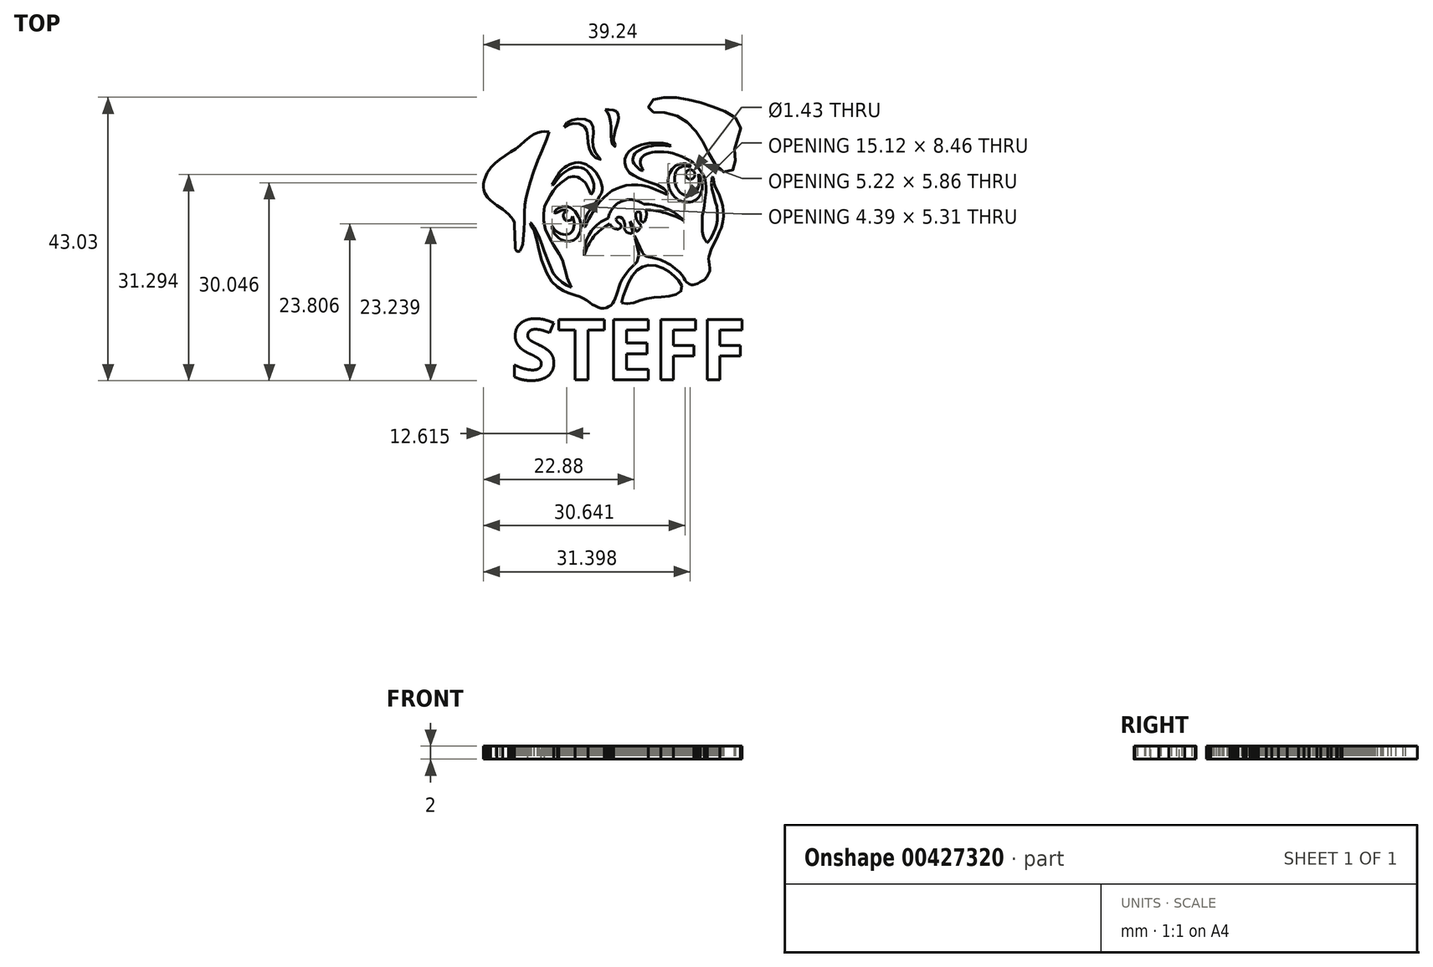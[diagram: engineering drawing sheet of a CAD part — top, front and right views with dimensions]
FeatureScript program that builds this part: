
annotation { "Feature Type Name" : "Feature", "Feature Type Description" : "" }
export const myFeature = defineFeature(function(context is Context, id is Id, definition is map)
    precondition{}
    {
        {
            var Q0;
            Q0=qCreatedBy(makeId("Top.planeOp"),FACE);
            var sketch = newSketch(context, id + "F0", { "sketchPlane" : qUnion([Q0])});
            skLineSegment(sketch, "E0", {"start": v(10.71, 26.9) * mm, "end": v(10.32, 25.78) * mm});
            skLineSegment(sketch, "E1", {"start": v(10.32, 25.78) * mm, "end": v(9.6, 24.09) * mm});
            skLineSegment(sketch, "E2", {"start": v(9.6, 24.09) * mm, "end": v(9, 22.63) * mm});
            skLineSegment(sketch, "E3", {"start": v(9, 22.63) * mm, "end": v(8.35, 20.88) * mm});
            skLineSegment(sketch, "E4", {"start": v(8.35, 20.88) * mm, "end": v(7.83, 19.32) * mm});
            skLineSegment(sketch, "E5", {"start": v(7.83, 19.32) * mm, "end": v(7.5, 18.15) * mm});
            skLineSegment(sketch, "E6", {"start": v(7.5, 18.15) * mm, "end": v(7.2, 16.98) * mm});
            skLineSegment(sketch, "E7", {"start": v(7.2, 16.98) * mm, "end": v(7.03, 15.9) * mm});
            skLineSegment(sketch, "E8", {"start": v(7.03, 15.9) * mm, "end": v(6.93, 14.65) * mm});
            skLineSegment(sketch, "E9", {"start": v(6.93, 14.65) * mm, "end": v(6.93, 13.4) * mm});
            skLineSegment(sketch, "E10", {"start": v(6.93, 13.4) * mm, "end": v(6.86, 12.03) * mm});
            skLineSegment(sketch, "E11", {"start": v(6.86, 12.03) * mm, "end": v(6.82, 11.32) * mm});
            skLineSegment(sketch, "E12", {"start": v(6.82, 11.32) * mm, "end": v(6.66, 9.88) * mm});
            skLineSegment(sketch, "E13", {"start": v(6.66, 9.88) * mm, "end": v(6.53, 9.37) * mm});
            skLineSegment(sketch, "E14", {"start": v(6.53, 9.37) * mm, "end": v(6.4, 9.06) * mm});
            skLineSegment(sketch, "E15", {"start": v(6.4, 9.06) * mm, "end": v(6.24, 8.83) * mm});
            skLineSegment(sketch, "E16", {"start": v(6.24, 8.83) * mm, "end": v(6.14, 8.77) * mm});
            skLineSegment(sketch, "E17", {"start": v(6.14, 8.77) * mm, "end": v(5.97, 8.75) * mm});
            skLineSegment(sketch, "E18", {"start": v(5.97, 8.75) * mm, "end": v(5.78, 8.8) * mm});
            skLineSegment(sketch, "E19", {"start": v(5.78, 8.8) * mm, "end": v(5.66, 8.95) * mm});
            skLineSegment(sketch, "E20", {"start": v(5.66, 8.95) * mm, "end": v(5.57, 9.16) * mm});
            skLineSegment(sketch, "E21", {"start": v(5.57, 9.16) * mm, "end": v(5.53, 9.55) * mm});
            skLineSegment(sketch, "E22", {"start": v(5.53, 9.55) * mm, "end": v(5.44, 12.77) * mm});
            skLineSegment(sketch, "E23", {"start": v(5.44, 12.77) * mm, "end": v(5.4, 13.16) * mm});
            skLineSegment(sketch, "E24", {"start": v(5.4, 13.16) * mm, "end": v(5.23, 13.6) * mm});
            skLineSegment(sketch, "E25", {"start": v(5.23, 13.6) * mm, "end": v(4.93, 14) * mm});
            skLineSegment(sketch, "E26", {"start": v(4.93, 14) * mm, "end": v(4.55, 14.4) * mm});
            skLineSegment(sketch, "E27", {"start": v(4.55, 14.4) * mm, "end": v(4.15, 14.73) * mm});
            skLineSegment(sketch, "E28", {"start": v(4.15, 14.73) * mm, "end": v(3.62, 15.16) * mm});
            skLineSegment(sketch, "E29", {"start": v(3.62, 15.16) * mm, "end": v(2.75, 15.77) * mm});
            skLineSegment(sketch, "E30", {"start": v(2.75, 15.77) * mm, "end": v(1.8, 16.54) * mm});
            skLineSegment(sketch, "E31", {"start": v(1.8, 16.54) * mm, "end": v(1.34, 16.97) * mm});
            skLineSegment(sketch, "E32", {"start": v(1.34, 16.97) * mm, "end": v(0.93, 17.65) * mm});
            skLineSegment(sketch, "E33", {"start": v(0.93, 17.65) * mm, "end": v(0.8, 18.1) * mm});
            skLineSegment(sketch, "E34", {"start": v(0.8, 18.1) * mm, "end": v(0.71, 18.48) * mm});
            skLineSegment(sketch, "E35", {"start": v(0.71, 18.48) * mm, "end": v(0.75, 19.06) * mm});
            skLineSegment(sketch, "E36", {"start": v(0.75, 19.06) * mm, "end": v(0.87, 19.56) * mm});
            skLineSegment(sketch, "E37", {"start": v(0.87, 19.56) * mm, "end": v(1.04, 20.05) * mm});
            skLineSegment(sketch, "E38", {"start": v(1.04, 20.05) * mm, "end": v(1.32, 20.73) * mm});
            skLineSegment(sketch, "E39", {"start": v(1.32, 20.73) * mm, "end": v(1.87, 21.5) * mm});
            skLineSegment(sketch, "E40", {"start": v(1.87, 21.5) * mm, "end": v(2.5, 22.16) * mm});
            skLineSegment(sketch, "E41", {"start": v(2.5, 22.16) * mm, "end": v(3.18, 22.75) * mm});
            skLineSegment(sketch, "E42", {"start": v(3.18, 22.75) * mm, "end": v(4.85, 23.86) * mm});
            skLineSegment(sketch, "E43", {"start": v(4.85, 23.86) * mm, "end": v(5.64, 24.35) * mm});
            skLineSegment(sketch, "E44", {"start": v(5.64, 24.35) * mm, "end": v(6.34, 24.92) * mm});
            skLineSegment(sketch, "E45", {"start": v(6.34, 24.92) * mm, "end": v(6.98, 25.53) * mm});
            skLineSegment(sketch, "E46", {"start": v(6.98, 25.53) * mm, "end": v(7.68, 26.08) * mm});
            skLineSegment(sketch, "E47", {"start": v(7.68, 26.08) * mm, "end": v(8.36, 26.56) * mm});
            skLineSegment(sketch, "E48", {"start": v(8.36, 26.56) * mm, "end": v(8.96, 26.8) * mm});
            skLineSegment(sketch, "E49", {"start": v(8.96, 26.8) * mm, "end": v(9.5, 26.95) * mm});
            skLineSegment(sketch, "E50", {"start": v(9.5, 26.95) * mm, "end": v(9.97, 26.97) * mm});
            skLineSegment(sketch, "E51", {"start": v(9.97, 26.97) * mm, "end": v(10.38, 26.95) * mm});
            skLineSegment(sketch, "E52", {"start": v(10.38, 26.95) * mm, "end": v(10.71, 26.9) * mm});
            skLineSegment(sketch, "E53", {"start": v(11.48, 14.68) * mm, "end": v(11.76, 15.13) * mm});
            skLineSegment(sketch, "E54", {"start": v(11.76, 15.13) * mm, "end": v(12.13, 15.39) * mm});
            skLineSegment(sketch, "E55", {"start": v(12.13, 15.39) * mm, "end": v(12.64, 15.57) * mm});
            skLineSegment(sketch, "E56", {"start": v(12.64, 15.57) * mm, "end": v(13.12, 15.6) * mm});
            skLineSegment(sketch, "E57", {"start": v(13.12, 15.6) * mm, "end": v(13.52, 15.57) * mm});
            skLineSegment(sketch, "E58", {"start": v(13.52, 15.57) * mm, "end": v(13.97, 15.39) * mm});
            skLineSegment(sketch, "E59", {"start": v(13.97, 15.39) * mm, "end": v(14.3, 15.13) * mm});
            skLineSegment(sketch, "E60", {"start": v(14.3, 15.13) * mm, "end": v(14.62, 14.84) * mm});
            skLineSegment(sketch, "E61", {"start": v(14.62, 14.84) * mm, "end": v(14.85, 14.53) * mm});
            skLineSegment(sketch, "E62", {"start": v(14.85, 14.53) * mm, "end": v(15.13, 14.06) * mm});
            skLineSegment(sketch, "E63", {"start": v(15.13, 14.06) * mm, "end": v(15.3, 13.65) * mm});
            skLineSegment(sketch, "E64", {"start": v(15.3, 13.65) * mm, "end": v(15.43, 13.2) * mm});
            skLineSegment(sketch, "E65", {"start": v(15.43, 13.2) * mm, "end": v(15.52, 12.58) * mm});
            skLineSegment(sketch, "E66", {"start": v(15.52, 12.58) * mm, "end": v(15.43, 11.9) * mm});
            skLineSegment(sketch, "E67", {"start": v(15.43, 11.9) * mm, "end": v(15.23, 11.3) * mm});
            skLineSegment(sketch, "E68", {"start": v(15.23, 11.3) * mm, "end": v(14.92, 10.84) * mm});
            skLineSegment(sketch, "E69", {"start": v(14.92, 10.84) * mm, "end": v(14.45, 10.5) * mm});
            skLineSegment(sketch, "E70", {"start": v(14.45, 10.5) * mm, "end": v(13.8, 10.3) * mm});
            skLineSegment(sketch, "E71", {"start": v(13.8, 10.3) * mm, "end": v(13.12, 10.37) * mm});
            skLineSegment(sketch, "E72", {"start": v(13.12, 10.37) * mm, "end": v(12.55, 10.56) * mm});
            skLineSegment(sketch, "E73", {"start": v(12.55, 10.56) * mm, "end": v(12.13, 10.82) * mm});
            skLineSegment(sketch, "E74", {"start": v(12.13, 10.82) * mm, "end": v(11.76, 11.16) * mm});
            skLineSegment(sketch, "E75", {"start": v(11.76, 11.16) * mm, "end": v(11.42, 11.56) * mm});
            skLineSegment(sketch, "E76", {"start": v(11.42, 11.56) * mm, "end": v(11.23, 12) * mm});
            skLineSegment(sketch, "E77", {"start": v(11.23, 12) * mm, "end": v(11.13, 12.34) * mm});
            skLineSegment(sketch, "E78", {"start": v(11.13, 12.34) * mm, "end": v(11.13, 12.63) * mm});
            skLineSegment(sketch, "E79", {"start": v(11.13, 12.63) * mm, "end": v(11.32, 12.37) * mm});
            skLineSegment(sketch, "E80", {"start": v(11.32, 12.37) * mm, "end": v(11.44, 12.16) * mm});
            skLineSegment(sketch, "E81", {"start": v(11.44, 12.16) * mm, "end": v(11.56, 12) * mm});
            skLineSegment(sketch, "E82", {"start": v(11.56, 12) * mm, "end": v(11.76, 11.81) * mm});
            skLineSegment(sketch, "E83", {"start": v(11.76, 11.81) * mm, "end": v(12, 11.67) * mm});
            skLineSegment(sketch, "E84", {"start": v(12, 11.67) * mm, "end": v(12.2, 11.54) * mm});
            skLineSegment(sketch, "E85", {"start": v(12.2, 11.54) * mm, "end": v(12.45, 11.43) * mm});
            skLineSegment(sketch, "E86", {"start": v(12.45, 11.43) * mm, "end": v(12.78, 11.35) * mm});
            skLineSegment(sketch, "E87", {"start": v(12.78, 11.35) * mm, "end": v(13.14, 11.33) * mm});
            skLineSegment(sketch, "E88", {"start": v(13.14, 11.33) * mm, "end": v(13.45, 11.37) * mm});
            skLineSegment(sketch, "E89", {"start": v(13.45, 11.37) * mm, "end": v(13.78, 11.47) * mm});
            skLineSegment(sketch, "E90", {"start": v(13.78, 11.47) * mm, "end": v(14.05, 11.66) * mm});
            skLineSegment(sketch, "E91", {"start": v(14.05, 11.66) * mm, "end": v(14.23, 11.9) * mm});
            skLineSegment(sketch, "E92", {"start": v(14.23, 11.9) * mm, "end": v(14.37, 12.2) * mm});
            skLineSegment(sketch, "E93", {"start": v(14.37, 12.2) * mm, "end": v(14.45, 12.5) * mm});
            skLineSegment(sketch, "E94", {"start": v(14.45, 12.5) * mm, "end": v(14.5, 12.82) * mm});
            skLineSegment(sketch, "E95", {"start": v(14.5, 12.82) * mm, "end": v(14.5, 13.12) * mm});
            skLineSegment(sketch, "E96", {"start": v(14.5, 13.12) * mm, "end": v(14.45, 13.43) * mm});
            skLineSegment(sketch, "E97", {"start": v(14.45, 13.43) * mm, "end": v(14.36, 13.71) * mm});
            skLineSegment(sketch, "E98", {"start": v(14.36, 13.71) * mm, "end": v(14.25, 14.1) * mm});
            skLineSegment(sketch, "E99", {"start": v(14.25, 14.1) * mm, "end": v(14.2, 13.94) * mm});
            skLineSegment(sketch, "E100", {"start": v(14.2, 13.94) * mm, "end": v(14.15, 13.72) * mm});
            skLineSegment(sketch, "E101", {"start": v(14.15, 13.72) * mm, "end": v(13.97, 13.52) * mm});
            skLineSegment(sketch, "E102", {"start": v(13.97, 13.52) * mm, "end": v(13.77, 13.44) * mm});
            skLineSegment(sketch, "E103", {"start": v(13.77, 13.44) * mm, "end": v(13.49, 13.42) * mm});
            skLineSegment(sketch, "E104", {"start": v(13.49, 13.42) * mm, "end": v(13.25, 13.48) * mm});
            skLineSegment(sketch, "E105", {"start": v(13.25, 13.48) * mm, "end": v(13.07, 13.59) * mm});
            skLineSegment(sketch, "E106", {"start": v(13.07, 13.59) * mm, "end": v(12.95, 13.78) * mm});
            skLineSegment(sketch, "E107", {"start": v(12.95, 13.78) * mm, "end": v(12.86, 14.09) * mm});
            skLineSegment(sketch, "E108", {"start": v(12.86, 14.09) * mm, "end": v(12.86, 14.4) * mm});
            skLineSegment(sketch, "E109", {"start": v(12.86, 14.4) * mm, "end": v(12.99, 14.6) * mm});
            skLineSegment(sketch, "E110", {"start": v(12.99, 14.6) * mm, "end": v(13.16, 14.77) * mm});
            skLineSegment(sketch, "E111", {"start": v(13.16, 14.77) * mm, "end": v(13.35, 14.82) * mm});
            skLineSegment(sketch, "E112", {"start": v(13.35, 14.82) * mm, "end": v(13.5, 14.82) * mm});
            skLineSegment(sketch, "E113", {"start": v(13.5, 14.82) * mm, "end": v(13.37, 15) * mm});
            skLineSegment(sketch, "E114", {"start": v(13.37, 15) * mm, "end": v(13.22, 15.03) * mm});
            skLineSegment(sketch, "E115", {"start": v(13.22, 15.03) * mm, "end": v(13, 15.03) * mm});
            skLineSegment(sketch, "E116", {"start": v(13, 15.03) * mm, "end": v(12.75, 15.03) * mm});
            skLineSegment(sketch, "E117", {"start": v(12.75, 15.03) * mm, "end": v(12.51, 14.96) * mm});
            skLineSegment(sketch, "E118", {"start": v(12.51, 14.96) * mm, "end": v(12.24, 14.85) * mm});
            skLineSegment(sketch, "E119", {"start": v(12.24, 14.85) * mm, "end": v(11.89, 14.7) * mm});
            skLineSegment(sketch, "E120", {"start": v(11.89, 14.7) * mm, "end": v(11.69, 14.64) * mm});
            skLineSegment(sketch, "E121", {"start": v(11.69, 14.64) * mm, "end": v(11.5, 14.64) * mm});
            skLineSegment(sketch, "E122", {"start": v(11.5, 14.64) * mm, "end": v(11.48, 14.68) * mm});
            skCircle(sketch, "E123", {"center": v(32.1, 20.44) * mm, "radius": 0.71 * mm});
            skLineSegment(sketch, "E124", {"start": v(32.18, 21.67) * mm, "end": v(31.86, 21.67) * mm});
            skLineSegment(sketch, "E125", {"start": v(31.86, 21.67) * mm, "end": v(31.65, 21.7) * mm});
            skLineSegment(sketch, "E126", {"start": v(31.65, 21.7) * mm, "end": v(31.35, 21.71) * mm});
            skLineSegment(sketch, "E127", {"start": v(31.35, 21.71) * mm, "end": v(31.13, 21.7) * mm});
            skLineSegment(sketch, "E128", {"start": v(31.13, 21.7) * mm, "end": v(30.87, 21.65) * mm});
            skLineSegment(sketch, "E129", {"start": v(30.87, 21.65) * mm, "end": v(30.63, 21.56) * mm});
            skLineSegment(sketch, "E130", {"start": v(30.63, 21.56) * mm, "end": v(30.45, 21.45) * mm});
            skLineSegment(sketch, "E131", {"start": v(30.45, 21.45) * mm, "end": v(30.33, 21.34) * mm});
            skLineSegment(sketch, "E132", {"start": v(30.33, 21.34) * mm, "end": v(30.2, 21.2) * mm});
            skLineSegment(sketch, "E133", {"start": v(30.2, 21.2) * mm, "end": v(30.08, 21.06) * mm});
            skLineSegment(sketch, "E134", {"start": v(30.08, 21.06) * mm, "end": v(29.95, 20.88) * mm});
            skLineSegment(sketch, "E135", {"start": v(29.95, 20.88) * mm, "end": v(29.88, 20.7) * mm});
            skLineSegment(sketch, "E136", {"start": v(29.88, 20.7) * mm, "end": v(29.82, 20.5) * mm});
            skLineSegment(sketch, "E137", {"start": v(29.82, 20.5) * mm, "end": v(29.77, 20.3) * mm});
            skLineSegment(sketch, "E138", {"start": v(29.77, 20.3) * mm, "end": v(29.73, 20.07) * mm});
            skLineSegment(sketch, "E139", {"start": v(29.73, 20.07) * mm, "end": v(29.71, 19.84) * mm});
            skLineSegment(sketch, "E140", {"start": v(29.71, 19.84) * mm, "end": v(29.71, 19.6) * mm});
            skLineSegment(sketch, "E141", {"start": v(29.71, 19.6) * mm, "end": v(29.73, 19.4) * mm});
            skLineSegment(sketch, "E142", {"start": v(29.73, 19.4) * mm, "end": v(29.75, 19.25) * mm});
            skLineSegment(sketch, "E143", {"start": v(29.75, 19.25) * mm, "end": v(29.8, 19.1) * mm});
            skLineSegment(sketch, "E144", {"start": v(29.8, 19.1) * mm, "end": v(29.84, 18.97) * mm});
            skLineSegment(sketch, "E145", {"start": v(29.84, 18.97) * mm, "end": v(29.95, 18.67) * mm});
            skLineSegment(sketch, "E146", {"start": v(29.95, 18.67) * mm, "end": v(30.07, 18.43) * mm});
            skLineSegment(sketch, "E147", {"start": v(30.07, 18.43) * mm, "end": v(30.22, 18.16) * mm});
            skLineSegment(sketch, "E148", {"start": v(30.22, 18.16) * mm, "end": v(30.39, 17.94) * mm});
            skLineSegment(sketch, "E149", {"start": v(30.39, 17.94) * mm, "end": v(30.59, 17.75) * mm});
            skLineSegment(sketch, "E150", {"start": v(30.59, 17.75) * mm, "end": v(30.81, 17.55) * mm});
            skLineSegment(sketch, "E151", {"start": v(30.81, 17.55) * mm, "end": v(31.06, 17.4) * mm});
            skLineSegment(sketch, "E152", {"start": v(31.06, 17.4) * mm, "end": v(31.3, 17.3) * mm});
            skLineSegment(sketch, "E153", {"start": v(31.3, 17.3) * mm, "end": v(31.6, 17.25) * mm});
            skLineSegment(sketch, "E154", {"start": v(31.6, 17.25) * mm, "end": v(31.95, 17.22) * mm});
            skLineSegment(sketch, "E155", {"start": v(31.95, 17.22) * mm, "end": v(32.33, 17.28) * mm});
            skLineSegment(sketch, "E156", {"start": v(32.33, 17.28) * mm, "end": v(32.62, 17.45) * mm});
            skLineSegment(sketch, "E157", {"start": v(32.62, 17.45) * mm, "end": v(32.86, 17.67) * mm});
            skLineSegment(sketch, "E158", {"start": v(32.86, 17.67) * mm, "end": v(33.1, 17.98) * mm});
            skLineSegment(sketch, "E159", {"start": v(33.1, 17.98) * mm, "end": v(33.23, 18.3) * mm});
            skLineSegment(sketch, "E160", {"start": v(33.23, 18.3) * mm, "end": v(33.36, 18.61) * mm});
            skLineSegment(sketch, "E161", {"start": v(33.36, 18.61) * mm, "end": v(33.42, 18.96) * mm});
            skLineSegment(sketch, "E162", {"start": v(33.42, 18.96) * mm, "end": v(33.42, 19.36) * mm});
            skLineSegment(sketch, "E163", {"start": v(33.42, 19.36) * mm, "end": v(33.4, 19.7) * mm});
            skLineSegment(sketch, "E164", {"start": v(33.4, 19.7) * mm, "end": v(33.33, 20.18) * mm});
            skLineSegment(sketch, "E165", {"start": v(33.33, 20.18) * mm, "end": v(33.33, 20.49) * mm});
            skLineSegment(sketch, "E166", {"start": v(33.33, 20.49) * mm, "end": v(33.42, 20.36) * mm});
            skLineSegment(sketch, "E167", {"start": v(33.42, 20.36) * mm, "end": v(33.6, 20.08) * mm});
            skLineSegment(sketch, "E168", {"start": v(33.6, 20.08) * mm, "end": v(33.77, 19.7) * mm});
            skLineSegment(sketch, "E169", {"start": v(33.77, 19.7) * mm, "end": v(33.87, 19.37) * mm});
            skLineSegment(sketch, "E170", {"start": v(33.87, 19.37) * mm, "end": v(33.96, 18.8) * mm});
            skLineSegment(sketch, "E171", {"start": v(33.96, 18.8) * mm, "end": v(33.91, 18.25) * mm});
            skLineSegment(sketch, "E172", {"start": v(33.91, 18.25) * mm, "end": v(33.77, 17.68) * mm});
            skLineSegment(sketch, "E173", {"start": v(33.77, 17.68) * mm, "end": v(33.6, 17.3) * mm});
            skLineSegment(sketch, "E174", {"start": v(33.6, 17.3) * mm, "end": v(33.3, 16.9) * mm});
            skLineSegment(sketch, "E175", {"start": v(33.3, 16.9) * mm, "end": v(33.01, 16.66) * mm});
            skLineSegment(sketch, "E176", {"start": v(33.01, 16.66) * mm, "end": v(32.67, 16.45) * mm});
            skLineSegment(sketch, "E177", {"start": v(32.67, 16.45) * mm, "end": v(32.38, 16.33) * mm});
            skLineSegment(sketch, "E178", {"start": v(32.38, 16.33) * mm, "end": v(32.07, 16.28) * mm});
            skLineSegment(sketch, "E179", {"start": v(32.07, 16.28) * mm, "end": v(31.75, 16.26) * mm});
            skLineSegment(sketch, "E180", {"start": v(31.75, 16.26) * mm, "end": v(31.45, 16.26) * mm});
            skLineSegment(sketch, "E181", {"start": v(31.45, 16.26) * mm, "end": v(31.18, 16.3) * mm});
            skLineSegment(sketch, "E182", {"start": v(31.18, 16.3) * mm, "end": v(30.91, 16.35) * mm});
            skLineSegment(sketch, "E183", {"start": v(30.91, 16.35) * mm, "end": v(30.6, 16.44) * mm});
            skLineSegment(sketch, "E184", {"start": v(30.6, 16.44) * mm, "end": v(30.33, 16.58) * mm});
            skLineSegment(sketch, "E185", {"start": v(30.33, 16.58) * mm, "end": v(30.12, 16.7) * mm});
            skLineSegment(sketch, "E186", {"start": v(30.12, 16.7) * mm, "end": v(29.9, 16.88) * mm});
            skLineSegment(sketch, "E187", {"start": v(29.9, 16.88) * mm, "end": v(29.72, 17.05) * mm});
            skLineSegment(sketch, "E188", {"start": v(29.72, 17.05) * mm, "end": v(29.55, 17.25) * mm});
            skLineSegment(sketch, "E189", {"start": v(29.55, 17.25) * mm, "end": v(29.39, 17.47) * mm});
            skLineSegment(sketch, "E190", {"start": v(29.39, 17.47) * mm, "end": v(29.27, 17.65) * mm});
            skLineSegment(sketch, "E191", {"start": v(29.27, 17.65) * mm, "end": v(29.16, 17.84) * mm});
            skLineSegment(sketch, "E192", {"start": v(29.16, 17.84) * mm, "end": v(29.03, 18.07) * mm});
            skLineSegment(sketch, "E193", {"start": v(29.03, 18.07) * mm, "end": v(28.9, 18.35) * mm});
            skLineSegment(sketch, "E194", {"start": v(28.9, 18.35) * mm, "end": v(28.83, 18.68) * mm});
            skLineSegment(sketch, "E195", {"start": v(28.83, 18.68) * mm, "end": v(28.78, 19.02) * mm});
            skLineSegment(sketch, "E196", {"start": v(28.78, 19.02) * mm, "end": v(28.74, 19.27) * mm});
            skLineSegment(sketch, "E197", {"start": v(28.74, 19.27) * mm, "end": v(28.74, 19.54) * mm});
            skLineSegment(sketch, "E198", {"start": v(28.74, 19.54) * mm, "end": v(28.78, 19.96) * mm});
            skLineSegment(sketch, "E199", {"start": v(28.78, 19.96) * mm, "end": v(28.87, 20.33) * mm});
            skLineSegment(sketch, "E200", {"start": v(28.87, 20.33) * mm, "end": v(29, 20.64) * mm});
            skLineSegment(sketch, "E201", {"start": v(29, 20.64) * mm, "end": v(29.17, 20.94) * mm});
            skLineSegment(sketch, "E202", {"start": v(29.17, 20.94) * mm, "end": v(29.39, 21.3) * mm});
            skLineSegment(sketch, "E203", {"start": v(29.39, 21.3) * mm, "end": v(29.6, 21.54) * mm});
            skLineSegment(sketch, "E204", {"start": v(29.6, 21.54) * mm, "end": v(29.87, 21.77) * mm});
            skLineSegment(sketch, "E205", {"start": v(29.87, 21.77) * mm, "end": v(30.17, 21.94) * mm});
            skLineSegment(sketch, "E206", {"start": v(30.17, 21.94) * mm, "end": v(30.56, 22.07) * mm});
            skLineSegment(sketch, "E207", {"start": v(30.56, 22.07) * mm, "end": v(31.03, 22.13) * mm});
            skLineSegment(sketch, "E208", {"start": v(31.03, 22.13) * mm, "end": v(31.41, 22.08) * mm});
            skLineSegment(sketch, "E209", {"start": v(31.41, 22.08) * mm, "end": v(31.73, 22) * mm});
            skLineSegment(sketch, "E210", {"start": v(31.73, 22) * mm, "end": v(32.11, 21.82) * mm});
            skLineSegment(sketch, "E211", {"start": v(32.11, 21.82) * mm, "end": v(32.2, 21.67) * mm});
            skLineSegment(sketch, "E212", {"start": v(32.2, 21.67) * mm, "end": v(32.18, 21.67) * mm});
            skLineSegment(sketch, "E213", {"start": v(23.61, 11.16) * mm, "end": v(24.3, 8.53) * mm});
            skLineSegment(sketch, "E214", {"start": v(24.3, 8.53) * mm, "end": v(24.3, 8.07) * mm});
            skLineSegment(sketch, "E215", {"start": v(24.3, 8.07) * mm, "end": v(24.18, 7.68) * mm});
            skLineSegment(sketch, "E216", {"start": v(24.18, 7.68) * mm, "end": v(24, 7.2) * mm});
            skLineSegment(sketch, "E217", {"start": v(24, 7.2) * mm, "end": v(23.63, 6.79) * mm});
            skLineSegment(sketch, "E218", {"start": v(23.63, 6.79) * mm, "end": v(23.22, 6.36) * mm});
            skLineSegment(sketch, "E219", {"start": v(23.22, 6.36) * mm, "end": v(22.83, 5.97) * mm});
            skLineSegment(sketch, "E220", {"start": v(22.83, 5.97) * mm, "end": v(22.42, 5.48) * mm});
            skLineSegment(sketch, "E221", {"start": v(22.42, 5.48) * mm, "end": v(22.1, 5.04) * mm});
            skLineSegment(sketch, "E222", {"start": v(22.1, 5.04) * mm, "end": v(21.8, 4.55) * mm});
            skLineSegment(sketch, "E223", {"start": v(21.8, 4.55) * mm, "end": v(21.51, 3.96) * mm});
            skLineSegment(sketch, "E224", {"start": v(21.51, 3.96) * mm, "end": v(21.3, 3.36) * mm});
            skLineSegment(sketch, "E225", {"start": v(21.3, 3.36) * mm, "end": v(21.1, 2.72) * mm});
            skLineSegment(sketch, "E226", {"start": v(21.1, 2.72) * mm, "end": v(20.94, 2.2) * mm});
            skLineSegment(sketch, "E227", {"start": v(20.94, 2.2) * mm, "end": v(20.73, 1.67) * mm});
            skLineSegment(sketch, "E228", {"start": v(20.73, 1.67) * mm, "end": v(20.54, 1.22) * mm});
            skLineSegment(sketch, "E229", {"start": v(20.54, 1.22) * mm, "end": v(20.36, 0.91) * mm});
            skLineSegment(sketch, "E230", {"start": v(20.36, 0.91) * mm, "end": v(20.1, 0.6) * mm});
            skLineSegment(sketch, "E231", {"start": v(20.1, 0.6) * mm, "end": v(19.72, 0.36) * mm});
            skLineSegment(sketch, "E232", {"start": v(19.72, 0.36) * mm, "end": v(19.42, 0.2) * mm});
            skLineSegment(sketch, "E233", {"start": v(19.42, 0.2) * mm, "end": v(19, 0.15) * mm});
            skLineSegment(sketch, "E234", {"start": v(19, 0.15) * mm, "end": v(18.59, 0.15) * mm});
            skLineSegment(sketch, "E235", {"start": v(18.59, 0.15) * mm, "end": v(18.16, 0.3) * mm});
            skLineSegment(sketch, "E236", {"start": v(18.16, 0.3) * mm, "end": v(17.7, 0.49) * mm});
            skLineSegment(sketch, "E237", {"start": v(17.7, 0.49) * mm, "end": v(17.23, 0.7) * mm});
            skLineSegment(sketch, "E238", {"start": v(17.23, 0.7) * mm, "end": v(16.9, 0.98) * mm});
            skLineSegment(sketch, "E239", {"start": v(23.61, 11.16) * mm, "end": v(24.87, 8.6) * mm});
            skLineSegment(sketch, "E240", {"start": v(24.87, 8.6) * mm, "end": v(25.05, 8.35) * mm});
            skLineSegment(sketch, "E241", {"start": v(25.05, 8.35) * mm, "end": v(25.25, 8.14) * mm});
            skLineSegment(sketch, "E242", {"start": v(25.25, 8.14) * mm, "end": v(25.47, 8) * mm});
            skLineSegment(sketch, "E243", {"start": v(25.47, 8) * mm, "end": v(25.71, 7.95) * mm});
            skLineSegment(sketch, "E244", {"start": v(25.71, 7.95) * mm, "end": v(26.04, 7.89) * mm});
            skLineSegment(sketch, "E245", {"start": v(26.04, 7.89) * mm, "end": v(26.37, 7.81) * mm});
            skLineSegment(sketch, "E246", {"start": v(26.37, 7.81) * mm, "end": v(26.66, 7.75) * mm});
            skLineSegment(sketch, "E247", {"start": v(26.66, 7.75) * mm, "end": v(27.15, 7.61) * mm});
            skLineSegment(sketch, "E248", {"start": v(27.15, 7.61) * mm, "end": v(27.56, 7.48) * mm});
            skLineSegment(sketch, "E249", {"start": v(27.56, 7.48) * mm, "end": v(27.97, 7.32) * mm});
            skLineSegment(sketch, "E250", {"start": v(27.97, 7.32) * mm, "end": v(28.3, 7.15) * mm});
            skLineSegment(sketch, "E251", {"start": v(28.3, 7.15) * mm, "end": v(28.72, 6.95) * mm});
            skLineSegment(sketch, "E252", {"start": v(28.72, 6.95) * mm, "end": v(29.08, 6.73) * mm});
            skLineSegment(sketch, "E253", {"start": v(29.08, 6.73) * mm, "end": v(29.45, 6.48) * mm});
            skLineSegment(sketch, "E254", {"start": v(29.45, 6.48) * mm, "end": v(29.78, 6.2) * mm});
            skLineSegment(sketch, "E255", {"start": v(29.78, 6.2) * mm, "end": v(30.11, 5.9) * mm});
            skLineSegment(sketch, "E256", {"start": v(30.11, 5.9) * mm, "end": v(30.43, 5.63) * mm});
            skLineSegment(sketch, "E257", {"start": v(30.43, 5.63) * mm, "end": v(30.72, 5.33) * mm});
            skLineSegment(sketch, "E258", {"start": v(30.72, 5.33) * mm, "end": v(30.95, 5.08) * mm});
            skLineSegment(sketch, "E259", {"start": v(30.95, 5.08) * mm, "end": v(31.16, 4.72) * mm});
            skLineSegment(sketch, "E260", {"start": v(31.16, 4.72) * mm, "end": v(31.33, 4.42) * mm});
            skLineSegment(sketch, "E261", {"start": v(31.33, 4.42) * mm, "end": v(31.53, 4.15) * mm});
            skLineSegment(sketch, "E262", {"start": v(31.53, 4.15) * mm, "end": v(31.75, 3.95) * mm});
            skLineSegment(sketch, "E263", {"start": v(31.75, 3.95) * mm, "end": v(31.97, 3.8) * mm});
            skLineSegment(sketch, "E264", {"start": v(31.97, 3.8) * mm, "end": v(32.27, 3.7) * mm});
            skLineSegment(sketch, "E265", {"start": v(32.27, 3.7) * mm, "end": v(32.55, 3.7) * mm});
            skLineSegment(sketch, "E266", {"start": v(32.55, 3.7) * mm, "end": v(32.81, 3.73) * mm});
            skLineSegment(sketch, "E267", {"start": v(16.9, 0.98) * mm, "end": v(16.41, 1.3) * mm});
            skLineSegment(sketch, "E268", {"start": v(16.41, 1.3) * mm, "end": v(15.84, 1.65) * mm});
            skLineSegment(sketch, "E269", {"start": v(15.84, 1.65) * mm, "end": v(15.34, 1.92) * mm});
            skLineSegment(sketch, "E270", {"start": v(15.34, 1.92) * mm, "end": v(14.69, 2.13) * mm});
            skLineSegment(sketch, "E271", {"start": v(14.69, 2.13) * mm, "end": v(14.15, 2.3) * mm});
            skLineSegment(sketch, "E272", {"start": v(14.15, 2.3) * mm, "end": v(13.54, 2.5) * mm});
            skLineSegment(sketch, "E273", {"start": v(13.54, 2.5) * mm, "end": v(12.86, 2.8) * mm});
            skLineSegment(sketch, "E274", {"start": v(12.86, 2.8) * mm, "end": v(11.94, 3.4) * mm});
            skLineSegment(sketch, "E275", {"start": v(11.94, 3.4) * mm, "end": v(11.07, 4.23) * mm});
            skLineSegment(sketch, "E276", {"start": v(11.07, 4.23) * mm, "end": v(10.3, 5.53) * mm});
            skLineSegment(sketch, "E277", {"start": v(10.3, 5.53) * mm, "end": v(9.58, 7.4) * mm});
            skLineSegment(sketch, "E278", {"start": v(9.58, 7.4) * mm, "end": v(9.2, 8.88) * mm});
            skLineSegment(sketch, "E279", {"start": v(9.2, 8.88) * mm, "end": v(8.86, 10.34) * mm});
            skLineSegment(sketch, "E280", {"start": v(8.86, 10.34) * mm, "end": v(8.38, 11.92) * mm});
            skLineSegment(sketch, "E281", {"start": v(8.38, 11.92) * mm, "end": v(7.94, 12.58) * mm});
            skLineSegment(sketch, "E282", {"start": v(7.94, 12.58) * mm, "end": v(7.8, 13.12) * mm});
            skLineSegment(sketch, "E283", {"start": v(7.8, 13.12) * mm, "end": v(7.93, 13.1) * mm});
            skLineSegment(sketch, "E284", {"start": v(7.93, 13.1) * mm, "end": v(8.43, 12.48) * mm});
            skLineSegment(sketch, "E285", {"start": v(8.43, 12.48) * mm, "end": v(9.11, 11.13) * mm});
            skLineSegment(sketch, "E286", {"start": v(9.11, 11.13) * mm, "end": v(9.63, 9.8) * mm});
            skLineSegment(sketch, "E287", {"start": v(9.63, 9.8) * mm, "end": v(9.93, 8.8) * mm});
            skLineSegment(sketch, "E288", {"start": v(9.93, 8.8) * mm, "end": v(10.61, 7.04) * mm});
            skLineSegment(sketch, "E289", {"start": v(10.61, 7.04) * mm, "end": v(11.33, 5.41) * mm});
            skLineSegment(sketch, "E290", {"start": v(11.33, 5.41) * mm, "end": v(11.9, 4.75) * mm});
            skLineSegment(sketch, "E291", {"start": v(11.9, 4.75) * mm, "end": v(12.67, 4.1) * mm});
            skLineSegment(sketch, "E292", {"start": v(12.67, 4.1) * mm, "end": v(13.33, 3.6) * mm});
            skLineSegment(sketch, "E293", {"start": v(13.33, 3.6) * mm, "end": v(14.03, 3.3) * mm});
            skLineSegment(sketch, "E294", {"start": v(14.03, 3.3) * mm, "end": v(13.42, 4.75) * mm});
            skLineSegment(sketch, "E295", {"start": v(13.42, 4.75) * mm, "end": v(13.23, 5.58) * mm});
            skLineSegment(sketch, "E296", {"start": v(13.23, 5.58) * mm, "end": v(12.98, 6.5) * mm});
            skLineSegment(sketch, "E297", {"start": v(12.98, 6.5) * mm, "end": v(12.72, 7.43) * mm});
            skLineSegment(sketch, "E298", {"start": v(12.72, 7.43) * mm, "end": v(12.23, 8.42) * mm});
            skLineSegment(sketch, "E299", {"start": v(12.23, 8.42) * mm, "end": v(11.8, 9.08) * mm});
            skLineSegment(sketch, "E300", {"start": v(11.8, 9.08) * mm, "end": v(11.33, 9.76) * mm});
            skLineSegment(sketch, "E301", {"start": v(11.33, 9.76) * mm, "end": v(10.75, 10.82) * mm});
            skLineSegment(sketch, "E302", {"start": v(10.75, 10.82) * mm, "end": v(10.1, 12.14) * mm});
            skLineSegment(sketch, "E303", {"start": v(10.1, 12.14) * mm, "end": v(9.85, 13.44) * mm});
            skLineSegment(sketch, "E304", {"start": v(9.85, 13.44) * mm, "end": v(9.85, 14.5) * mm});
            skLineSegment(sketch, "E305", {"start": v(9.85, 14.5) * mm, "end": v(9.98, 15.64) * mm});
            skLineSegment(sketch, "E306", {"start": v(9.98, 15.64) * mm, "end": v(10.43, 16.46) * mm});
            skLineSegment(sketch, "E307", {"start": v(10.43, 16.46) * mm, "end": v(10.86, 17.3) * mm});
            skLineSegment(sketch, "E308", {"start": v(10.86, 17.3) * mm, "end": v(11.32, 17.97) * mm});
            skLineSegment(sketch, "E309", {"start": v(11.32, 17.97) * mm, "end": v(11.8, 18.56) * mm});
            skLineSegment(sketch, "E310", {"start": v(11.8, 18.56) * mm, "end": v(12.42, 19.14) * mm});
            skLineSegment(sketch, "E311", {"start": v(12.42, 19.14) * mm, "end": v(13.14, 19.63) * mm});
            skLineSegment(sketch, "E312", {"start": v(13.14, 19.63) * mm, "end": v(13.64, 19.98) * mm});
            skLineSegment(sketch, "E313", {"start": v(13.64, 19.98) * mm, "end": v(14.22, 20.15) * mm});
            skLineSegment(sketch, "E314", {"start": v(14.22, 20.15) * mm, "end": v(14.63, 20.15) * mm});
            skLineSegment(sketch, "E315", {"start": v(14.63, 20.15) * mm, "end": v(15.04, 20.04) * mm});
            skLineSegment(sketch, "E316", {"start": v(15.04, 20.04) * mm, "end": v(15.33, 19.88) * mm});
            skLineSegment(sketch, "E317", {"start": v(15.33, 19.88) * mm, "end": v(15.78, 19.58) * mm});
            skLineSegment(sketch, "E318", {"start": v(15.78, 19.58) * mm, "end": v(16.2, 19.16) * mm});
            skLineSegment(sketch, "E319", {"start": v(16.2, 19.16) * mm, "end": v(16.52, 18.57) * mm});
            skLineSegment(sketch, "E320", {"start": v(16.52, 18.57) * mm, "end": v(16.77, 18.07) * mm});
            skLineSegment(sketch, "E321", {"start": v(16.77, 18.07) * mm, "end": v(16.91, 17.67) * mm});
            skLineSegment(sketch, "E322", {"start": v(16.91, 17.67) * mm, "end": v(17.04, 17.49) * mm});
            skLineSegment(sketch, "E323", {"start": v(17.04, 17.49) * mm, "end": v(17.15, 17.52) * mm});
            skLineSegment(sketch, "E324", {"start": v(17.15, 17.52) * mm, "end": v(17.34, 17.76) * mm});
            skLineSegment(sketch, "E325", {"start": v(17.34, 17.76) * mm, "end": v(17.47, 18.4) * mm});
            skLineSegment(sketch, "E326", {"start": v(17.47, 18.4) * mm, "end": v(17.47, 19) * mm});
            skLineSegment(sketch, "E327", {"start": v(17.47, 19) * mm, "end": v(17.25, 19.78) * mm});
            skLineSegment(sketch, "E328", {"start": v(17.25, 19.78) * mm, "end": v(17, 20.24) * mm});
            skLineSegment(sketch, "E329", {"start": v(17, 20.24) * mm, "end": v(16.68, 20.69) * mm});
            skLineSegment(sketch, "E330", {"start": v(16.68, 20.69) * mm, "end": v(16.39, 21) * mm});
            skLineSegment(sketch, "E331", {"start": v(16.39, 21) * mm, "end": v(15.98, 21.32) * mm});
            skLineSegment(sketch, "E332", {"start": v(15.98, 21.32) * mm, "end": v(15.57, 21.47) * mm});
            skLineSegment(sketch, "E333", {"start": v(15.57, 21.47) * mm, "end": v(15.2, 21.56) * mm});
            skLineSegment(sketch, "E334", {"start": v(15.2, 21.56) * mm, "end": v(14.84, 21.56) * mm});
            skLineSegment(sketch, "E335", {"start": v(14.84, 21.56) * mm, "end": v(14.43, 21.51) * mm});
            skLineSegment(sketch, "E336", {"start": v(14.43, 21.51) * mm, "end": v(14.1, 21.4) * mm});
            skLineSegment(sketch, "E337", {"start": v(14.1, 21.4) * mm, "end": v(13.65, 21.24) * mm});
            skLineSegment(sketch, "E338", {"start": v(13.65, 21.24) * mm, "end": v(13.26, 20.96) * mm});
            skLineSegment(sketch, "E339", {"start": v(13.26, 20.96) * mm, "end": v(12.91, 20.72) * mm});
            skLineSegment(sketch, "E340", {"start": v(12.91, 20.72) * mm, "end": v(12.62, 20.47) * mm});
            skLineSegment(sketch, "E341", {"start": v(12.62, 20.47) * mm, "end": v(12.3, 20.13) * mm});
            skLineSegment(sketch, "E342", {"start": v(12.3, 20.13) * mm, "end": v(12.04, 19.81) * mm});
            skLineSegment(sketch, "E343", {"start": v(12.04, 19.81) * mm, "end": v(11.8, 19.52) * mm});
            skLineSegment(sketch, "E344", {"start": v(11.8, 19.52) * mm, "end": v(11.53, 19.14) * mm});
            skLineSegment(sketch, "E345", {"start": v(11.53, 19.14) * mm, "end": v(11.22, 18.77) * mm});
            skLineSegment(sketch, "E346", {"start": v(11.22, 18.77) * mm, "end": v(11.13, 18.84) * mm});
            skLineSegment(sketch, "E347", {"start": v(11.13, 18.84) * mm, "end": v(11.52, 19.52) * mm});
            skLineSegment(sketch, "E348", {"start": v(11.52, 19.52) * mm, "end": v(11.89, 20.15) * mm});
            skLineSegment(sketch, "E349", {"start": v(11.89, 20.15) * mm, "end": v(12.3, 20.84) * mm});
            skLineSegment(sketch, "E350", {"start": v(12.3, 20.84) * mm, "end": v(12.68, 21.2) * mm});
            skLineSegment(sketch, "E351", {"start": v(12.68, 21.2) * mm, "end": v(13.06, 21.5) * mm});
            skLineSegment(sketch, "E352", {"start": v(13.06, 21.5) * mm, "end": v(13.39, 21.75) * mm});
            skLineSegment(sketch, "E353", {"start": v(13.39, 21.75) * mm, "end": v(13.78, 21.98) * mm});
            skLineSegment(sketch, "E354", {"start": v(13.78, 21.98) * mm, "end": v(14.17, 22.13) * mm});
            skLineSegment(sketch, "E355", {"start": v(14.17, 22.13) * mm, "end": v(14.65, 22.24) * mm});
            skLineSegment(sketch, "E356", {"start": v(14.65, 22.24) * mm, "end": v(15.1, 22.29) * mm});
            skLineSegment(sketch, "E357", {"start": v(15.1, 22.29) * mm, "end": v(15.5, 22.24) * mm});
            skLineSegment(sketch, "E358", {"start": v(15.5, 22.24) * mm, "end": v(15.97, 22.13) * mm});
            skLineSegment(sketch, "E359", {"start": v(15.97, 22.13) * mm, "end": v(16.37, 21.96) * mm});
            skLineSegment(sketch, "E360", {"start": v(16.37, 21.96) * mm, "end": v(16.68, 21.75) * mm});
            skLineSegment(sketch, "E361", {"start": v(16.68, 21.75) * mm, "end": v(17.1, 21.45) * mm});
            skLineSegment(sketch, "E362", {"start": v(17.1, 21.45) * mm, "end": v(17.46, 21.1) * mm});
            skLineSegment(sketch, "E363", {"start": v(17.46, 21.1) * mm, "end": v(17.78, 20.75) * mm});
            skLineSegment(sketch, "E364", {"start": v(17.78, 20.75) * mm, "end": v(18.07, 20.34) * mm});
            skLineSegment(sketch, "E365", {"start": v(18.07, 20.34) * mm, "end": v(18.3, 19.9) * mm});
            skLineSegment(sketch, "E366", {"start": v(18.3, 19.9) * mm, "end": v(18.5, 19.49) * mm});
            skLineSegment(sketch, "E367", {"start": v(18.5, 19.49) * mm, "end": v(18.65, 19.01) * mm});
            skLineSegment(sketch, "E368", {"start": v(18.65, 19.01) * mm, "end": v(18.73, 18.54) * mm});
            skLineSegment(sketch, "E369", {"start": v(18.73, 18.54) * mm, "end": v(18.73, 18.08) * mm});
            skLineSegment(sketch, "E370", {"start": v(18.73, 18.08) * mm, "end": v(18.6, 17.62) * mm});
            skLineSegment(sketch, "E371", {"start": v(18.6, 17.62) * mm, "end": v(18.38, 17.2) * mm});
            skLineSegment(sketch, "E372", {"start": v(18.38, 17.2) * mm, "end": v(18.13, 16.8) * mm});
            skLineSegment(sketch, "E373", {"start": v(18.13, 16.8) * mm, "end": v(17.85, 16.4) * mm});
            skLineSegment(sketch, "E374", {"start": v(17.85, 16.4) * mm, "end": v(17.5, 15.9) * mm});
            skLineSegment(sketch, "E375", {"start": v(17.5, 15.9) * mm, "end": v(17.15, 15.44) * mm});
            skLineSegment(sketch, "E376", {"start": v(17.15, 15.44) * mm, "end": v(16.91, 15.09) * mm});
            skLineSegment(sketch, "E377", {"start": v(16.91, 15.09) * mm, "end": v(16.62, 14.7) * mm});
            skLineSegment(sketch, "E378", {"start": v(16.62, 14.7) * mm, "end": v(16.43, 14.3) * mm});
            skLineSegment(sketch, "E379", {"start": v(16.43, 14.3) * mm, "end": v(16.19, 13.86) * mm});
            skLineSegment(sketch, "E380", {"start": v(16.19, 13.86) * mm, "end": v(16.04, 13.42) * mm});
            skLineSegment(sketch, "E381", {"start": v(16.04, 13.42) * mm, "end": v(15.94, 12.98) * mm});
            skLineSegment(sketch, "E382", {"start": v(15.94, 12.98) * mm, "end": v(15.94, 12.6) * mm});
            skLineSegment(sketch, "E383", {"start": v(15.94, 12.6) * mm, "end": v(15.97, 12.5) * mm});
            skLineSegment(sketch, "E384", {"start": v(15.97, 12.5) * mm, "end": v(16.12, 12.5) * mm});
            skLineSegment(sketch, "E385", {"start": v(16.12, 12.5) * mm, "end": v(16.25, 12.71) * mm});
            skLineSegment(sketch, "E386", {"start": v(16.25, 12.71) * mm, "end": v(16.44, 13.08) * mm});
            skLineSegment(sketch, "E387", {"start": v(16.44, 13.08) * mm, "end": v(16.7, 13.7) * mm});
            skLineSegment(sketch, "E388", {"start": v(16.7, 13.7) * mm, "end": v(17.04, 14.22) * mm});
            skLineSegment(sketch, "E389", {"start": v(17.04, 14.22) * mm, "end": v(17.37, 14.83) * mm});
            skLineSegment(sketch, "E390", {"start": v(17.37, 14.83) * mm, "end": v(17.88, 15.64) * mm});
            skLineSegment(sketch, "E391", {"start": v(17.88, 15.64) * mm, "end": v(18.39, 16.3) * mm});
            skLineSegment(sketch, "E392", {"start": v(18.39, 16.3) * mm, "end": v(18.94, 16.88) * mm});
            skLineSegment(sketch, "E393", {"start": v(18.94, 16.88) * mm, "end": v(19.56, 17.49) * mm});
            skLineSegment(sketch, "E394", {"start": v(19.56, 17.49) * mm, "end": v(20.24, 17.96) * mm});
            skLineSegment(sketch, "E395", {"start": v(20.24, 17.96) * mm, "end": v(20.94, 18.32) * mm});
            skLineSegment(sketch, "E396", {"start": v(20.94, 18.32) * mm, "end": v(21.6, 18.58) * mm});
            skLineSegment(sketch, "E397", {"start": v(21.6, 18.58) * mm, "end": v(22.35, 18.79) * mm});
            skLineSegment(sketch, "E398", {"start": v(22.35, 18.79) * mm, "end": v(23.23, 18.9) * mm});
            skLineSegment(sketch, "E399", {"start": v(23.23, 18.9) * mm, "end": v(24.12, 18.9) * mm});
            skLineSegment(sketch, "E400", {"start": v(24.12, 18.9) * mm, "end": v(24.82, 18.79) * mm});
            skLineSegment(sketch, "E401", {"start": v(24.82, 18.79) * mm, "end": v(25.66, 18.6) * mm});
            skLineSegment(sketch, "E402", {"start": v(25.66, 18.6) * mm, "end": v(26.4, 18.34) * mm});
            skLineSegment(sketch, "E403", {"start": v(26.4, 18.34) * mm, "end": v(26.97, 18.08) * mm});
            skLineSegment(sketch, "E404", {"start": v(26.97, 18.08) * mm, "end": v(27.59, 17.83) * mm});
            skLineSegment(sketch, "E405", {"start": v(27.59, 17.83) * mm, "end": v(28.03, 17.63) * mm});
            skLineSegment(sketch, "E406", {"start": v(28.03, 17.63) * mm, "end": v(28.4, 17.46) * mm});
            skLineSegment(sketch, "E407", {"start": v(28.4, 17.46) * mm, "end": v(28.66, 17.46) * mm});
            skLineSegment(sketch, "E408", {"start": v(28.66, 17.46) * mm, "end": v(28.66, 17.66) * mm});
            skLineSegment(sketch, "E409", {"start": v(28.66, 17.66) * mm, "end": v(28.07, 18.29) * mm});
            skLineSegment(sketch, "E410", {"start": v(28.07, 18.29) * mm, "end": v(27.11, 18.84) * mm});
            skLineSegment(sketch, "E411", {"start": v(27.11, 18.84) * mm, "end": v(26.2, 19.16) * mm});
            skLineSegment(sketch, "E412", {"start": v(26.2, 19.16) * mm, "end": v(25.28, 19.51) * mm});
            skLineSegment(sketch, "E413", {"start": v(25.28, 19.51) * mm, "end": v(24.33, 19.87) * mm});
            skLineSegment(sketch, "E414", {"start": v(24.33, 19.87) * mm, "end": v(23.5, 20.31) * mm});
            skLineSegment(sketch, "E415", {"start": v(23.5, 20.31) * mm, "end": v(22.91, 20.73) * mm});
            skLineSegment(sketch, "E416", {"start": v(22.91, 20.73) * mm, "end": v(22.4, 21.48) * mm});
            skLineSegment(sketch, "E417", {"start": v(22.4, 21.48) * mm, "end": v(22.2, 22.15) * mm});
            skLineSegment(sketch, "E418", {"start": v(22.2, 22.15) * mm, "end": v(22.2, 22.83) * mm});
            skLineSegment(sketch, "E419", {"start": v(22.2, 22.83) * mm, "end": v(22.52, 23.59) * mm});
            skLineSegment(sketch, "E420", {"start": v(22.52, 23.59) * mm, "end": v(22.9, 24) * mm});
            skLineSegment(sketch, "E421", {"start": v(22.9, 24) * mm, "end": v(23.4, 24.4) * mm});
            skLineSegment(sketch, "E422", {"start": v(23.4, 24.4) * mm, "end": v(23.92, 24.67) * mm});
            skLineSegment(sketch, "E423", {"start": v(23.92, 24.67) * mm, "end": v(24.64, 24.96) * mm});
            skLineSegment(sketch, "E424", {"start": v(24.64, 24.96) * mm, "end": v(25.24, 25.11) * mm});
            skLineSegment(sketch, "E425", {"start": v(25.24, 25.11) * mm, "end": v(25.89, 25.23) * mm});
            skLineSegment(sketch, "E426", {"start": v(25.89, 25.23) * mm, "end": v(26.63, 25.23) * mm});
            skLineSegment(sketch, "E427", {"start": v(26.63, 25.23) * mm, "end": v(27.33, 25.23) * mm});
            skLineSegment(sketch, "E428", {"start": v(27.33, 25.23) * mm, "end": v(27.95, 25.2) * mm});
            skLineSegment(sketch, "E429", {"start": v(27.95, 25.2) * mm, "end": v(28.58, 25.07) * mm});
            skLineSegment(sketch, "E430", {"start": v(28.58, 25.07) * mm, "end": v(29.16, 24.86) * mm});
            skLineSegment(sketch, "E431", {"start": v(29.16, 24.86) * mm, "end": v(29.13, 24.75) * mm});
            skLineSegment(sketch, "E432", {"start": v(29.13, 24.75) * mm, "end": v(28.82, 24.75) * mm});
            skLineSegment(sketch, "E433", {"start": v(28.82, 24.75) * mm, "end": v(28.32, 24.86) * mm});
            skLineSegment(sketch, "E434", {"start": v(28.32, 24.86) * mm, "end": v(27.85, 24.9) * mm});
            skLineSegment(sketch, "E435", {"start": v(27.85, 24.9) * mm, "end": v(27.28, 24.9) * mm});
            skLineSegment(sketch, "E436", {"start": v(27.28, 24.9) * mm, "end": v(26.75, 24.87) * mm});
            skLineSegment(sketch, "E437", {"start": v(26.75, 24.87) * mm, "end": v(26.25, 24.8) * mm});
            skLineSegment(sketch, "E438", {"start": v(26.25, 24.8) * mm, "end": v(25.73, 24.69) * mm});
            skLineSegment(sketch, "E439", {"start": v(25.73, 24.69) * mm, "end": v(25.34, 24.58) * mm});
            skLineSegment(sketch, "E440", {"start": v(25.34, 24.58) * mm, "end": v(24.96, 24.46) * mm});
            skLineSegment(sketch, "E441", {"start": v(24.96, 24.46) * mm, "end": v(24.7, 24.32) * mm});
            skLineSegment(sketch, "E442", {"start": v(24.7, 24.32) * mm, "end": v(24.38, 24.16) * mm});
            skLineSegment(sketch, "E443", {"start": v(24.38, 24.16) * mm, "end": v(23.98, 23.9) * mm});
            skLineSegment(sketch, "E444", {"start": v(23.98, 23.9) * mm, "end": v(23.72, 23.65) * mm});
            skLineSegment(sketch, "E445", {"start": v(23.72, 23.65) * mm, "end": v(23.54, 23.34) * mm});
            skLineSegment(sketch, "E446", {"start": v(23.54, 23.34) * mm, "end": v(23.44, 23.05) * mm});
            skLineSegment(sketch, "E447", {"start": v(23.44, 23.05) * mm, "end": v(23.4, 22.73) * mm});
            skLineSegment(sketch, "E448", {"start": v(23.4, 22.73) * mm, "end": v(23.4, 22.43) * mm});
            skLineSegment(sketch, "E449", {"start": v(23.4, 22.43) * mm, "end": v(23.57, 22.1) * mm});
            skLineSegment(sketch, "E450", {"start": v(23.57, 22.1) * mm, "end": v(23.82, 21.77) * mm});
            skLineSegment(sketch, "E451", {"start": v(23.82, 21.77) * mm, "end": v(24.13, 21.47) * mm});
            skLineSegment(sketch, "E452", {"start": v(24.13, 21.47) * mm, "end": v(24.41, 21.24) * mm});
            skLineSegment(sketch, "E453", {"start": v(24.41, 21.24) * mm, "end": v(24.68, 21.07) * mm});
            skLineSegment(sketch, "E454", {"start": v(24.68, 21.07) * mm, "end": v(24.81, 21.02) * mm});
            skLineSegment(sketch, "E455", {"start": v(24.81, 21.02) * mm, "end": v(24.9, 21.11) * mm});
            skLineSegment(sketch, "E456", {"start": v(24.9, 21.11) * mm, "end": v(24.9, 21.26) * mm});
            skLineSegment(sketch, "E457", {"start": v(24.9, 21.26) * mm, "end": v(24.8, 21.47) * mm});
            skLineSegment(sketch, "E458", {"start": v(24.8, 21.47) * mm, "end": v(24.68, 21.69) * mm});
            skLineSegment(sketch, "E459", {"start": v(24.68, 21.69) * mm, "end": v(24.56, 22.12) * mm});
            skLineSegment(sketch, "E460", {"start": v(24.56, 22.12) * mm, "end": v(24.56, 22.5) * mm});
            skLineSegment(sketch, "E461", {"start": v(24.56, 22.5) * mm, "end": v(24.66, 22.9) * mm});
            skLineSegment(sketch, "E462", {"start": v(24.66, 22.9) * mm, "end": v(24.84, 23.15) * mm});
            skLineSegment(sketch, "E463", {"start": v(24.84, 23.15) * mm, "end": v(25.12, 23.4) * mm});
            skLineSegment(sketch, "E464", {"start": v(25.12, 23.4) * mm, "end": v(25.5, 23.59) * mm});
            skLineSegment(sketch, "E465", {"start": v(25.5, 23.59) * mm, "end": v(25.88, 23.72) * mm});
            skLineSegment(sketch, "E466", {"start": v(25.88, 23.72) * mm, "end": v(26.3, 23.82) * mm});
            skLineSegment(sketch, "E467", {"start": v(26.3, 23.82) * mm, "end": v(26.72, 23.9) * mm});
            skLineSegment(sketch, "E468", {"start": v(26.72, 23.9) * mm, "end": v(27.11, 23.9) * mm});
            skLineSegment(sketch, "E469", {"start": v(27.11, 23.9) * mm, "end": v(27.54, 23.9) * mm});
            skLineSegment(sketch, "E470", {"start": v(27.54, 23.9) * mm, "end": v(28.09, 23.9) * mm});
            skLineSegment(sketch, "E471", {"start": v(28.09, 23.9) * mm, "end": v(28.78, 23.8) * mm});
            skLineSegment(sketch, "E472", {"start": v(28.78, 23.8) * mm, "end": v(29.42, 23.68) * mm});
            skLineSegment(sketch, "E473", {"start": v(29.42, 23.68) * mm, "end": v(30.06, 23.44) * mm});
            skLineSegment(sketch, "E474", {"start": v(30.06, 23.44) * mm, "end": v(30.8, 23.18) * mm});
            skLineSegment(sketch, "E475", {"start": v(30.8, 23.18) * mm, "end": v(31.47, 22.89) * mm});
            skLineSegment(sketch, "E476", {"start": v(31.47, 22.89) * mm, "end": v(31.98, 22.61) * mm});
            skLineSegment(sketch, "E477", {"start": v(31.98, 22.61) * mm, "end": v(32.46, 22.28) * mm});
            skLineSegment(sketch, "E478", {"start": v(32.46, 22.28) * mm, "end": v(32.94, 21.89) * mm});
            skLineSegment(sketch, "E479", {"start": v(32.94, 21.89) * mm, "end": v(33.4, 21.37) * mm});
            skLineSegment(sketch, "E480", {"start": v(33.4, 21.37) * mm, "end": v(33.67, 20.98) * mm});
            skLineSegment(sketch, "E481", {"start": v(33.67, 20.98) * mm, "end": v(34, 20.54) * mm});
            skLineSegment(sketch, "E482", {"start": v(34, 20.54) * mm, "end": v(34.23, 20.07) * mm});
            skLineSegment(sketch, "E483", {"start": v(34.23, 20.07) * mm, "end": v(34.38, 19.6) * mm});
            skLineSegment(sketch, "E484", {"start": v(34.38, 19.6) * mm, "end": v(34.45, 19.12) * mm});
            skLineSegment(sketch, "E485", {"start": v(34.45, 19.12) * mm, "end": v(34.5, 18.6) * mm});
            skLineSegment(sketch, "E486", {"start": v(34.5, 18.6) * mm, "end": v(34.5, 18.17) * mm});
            skLineSegment(sketch, "E487", {"start": v(34.5, 18.17) * mm, "end": v(34.5, 17.71) * mm});
            skLineSegment(sketch, "E488", {"start": v(34.5, 17.71) * mm, "end": v(34.38, 16.96) * mm});
            skLineSegment(sketch, "E489", {"start": v(34.38, 16.96) * mm, "end": v(34.3, 16.38) * mm});
            skLineSegment(sketch, "E490", {"start": v(34.3, 16.38) * mm, "end": v(34.23, 15.73) * mm});
            skLineSegment(sketch, "E491", {"start": v(34.23, 15.73) * mm, "end": v(34.13, 14.93) * mm});
            skLineSegment(sketch, "E492", {"start": v(34.13, 14.93) * mm, "end": v(33.96, 14.26) * mm});
            skLineSegment(sketch, "E493", {"start": v(33.96, 14.26) * mm, "end": v(33.96, 13.32) * mm});
            skLineSegment(sketch, "E494", {"start": v(33.96, 13.32) * mm, "end": v(33.96, 12.46) * mm});
            skLineSegment(sketch, "E495", {"start": v(33.96, 12.46) * mm, "end": v(33.96, 11.8) * mm});
            skLineSegment(sketch, "E496", {"start": v(33.96, 11.8) * mm, "end": v(34.08, 11.2) * mm});
            skLineSegment(sketch, "E497", {"start": v(34.08, 11.2) * mm, "end": v(34.23, 10.7) * mm});
            skLineSegment(sketch, "E498", {"start": v(34.23, 10.7) * mm, "end": v(34.5, 10.34) * mm});
            skLineSegment(sketch, "E499", {"start": v(34.5, 10.34) * mm, "end": v(34.64, 10.12) * mm});
            skLineSegment(sketch, "E500", {"start": v(34.64, 10.12) * mm, "end": v(34.78, 10.16) * mm});
            skLineSegment(sketch, "E501", {"start": v(34.78, 10.16) * mm, "end": v(35.14, 10.64) * mm});
            skLineSegment(sketch, "E502", {"start": v(35.14, 10.64) * mm, "end": v(35.36, 11.06) * mm});
            skLineSegment(sketch, "E503", {"start": v(35.36, 11.06) * mm, "end": v(35.65, 11.64) * mm});
            skLineSegment(sketch, "E504", {"start": v(35.65, 11.64) * mm, "end": v(35.89, 12.2) * mm});
            skLineSegment(sketch, "E505", {"start": v(35.89, 12.2) * mm, "end": v(36.09, 12.8) * mm});
            skLineSegment(sketch, "E506", {"start": v(36.09, 12.8) * mm, "end": v(36.2, 13.48) * mm});
            skLineSegment(sketch, "E507", {"start": v(36.2, 13.48) * mm, "end": v(36.24, 14.2) * mm});
            skLineSegment(sketch, "E508", {"start": v(36.24, 14.2) * mm, "end": v(36.24, 14.82) * mm});
            skLineSegment(sketch, "E509", {"start": v(36.24, 14.82) * mm, "end": v(36.14, 15.65) * mm});
            skLineSegment(sketch, "E510", {"start": v(36.14, 15.65) * mm, "end": v(35.92, 16.35) * mm});
            skLineSegment(sketch, "E511", {"start": v(35.92, 16.35) * mm, "end": v(35.66, 17.4) * mm});
            skLineSegment(sketch, "E512", {"start": v(35.66, 17.4) * mm, "end": v(35.4, 18.25) * mm});
            skLineSegment(sketch, "E513", {"start": v(35.4, 18.25) * mm, "end": v(35.35, 19) * mm});
            skLineSegment(sketch, "E514", {"start": v(35.35, 19) * mm, "end": v(35.4, 20.03) * mm});
            skLineSegment(sketch, "E515", {"start": v(35.4, 20.03) * mm, "end": v(35.54, 20.07) * mm});
            skLineSegment(sketch, "E516", {"start": v(35.54, 20.07) * mm, "end": v(35.63, 19.9) * mm});
            skLineSegment(sketch, "E517", {"start": v(35.63, 19.9) * mm, "end": v(35.67, 19.58) * mm});
            skLineSegment(sketch, "E518", {"start": v(35.67, 19.58) * mm, "end": v(35.73, 19.1) * mm});
            skLineSegment(sketch, "E519", {"start": v(35.73, 19.1) * mm, "end": v(35.89, 18.56) * mm});
            skLineSegment(sketch, "E520", {"start": v(35.89, 18.56) * mm, "end": v(36.14, 18.08) * mm});
            skLineSegment(sketch, "E521", {"start": v(36.14, 18.08) * mm, "end": v(36.44, 17.5) * mm});
            skLineSegment(sketch, "E522", {"start": v(36.44, 17.5) * mm, "end": v(36.66, 16.9) * mm});
            skLineSegment(sketch, "E523", {"start": v(36.66, 16.9) * mm, "end": v(36.85, 16.3) * mm});
            skLineSegment(sketch, "E524", {"start": v(36.85, 16.3) * mm, "end": v(37.04, 15.71) * mm});
            skLineSegment(sketch, "E525", {"start": v(37.04, 15.71) * mm, "end": v(37.13, 14.95) * mm});
            skLineSegment(sketch, "E526", {"start": v(37.13, 14.95) * mm, "end": v(37.18, 14.11) * mm});
            skLineSegment(sketch, "E527", {"start": v(37.18, 14.11) * mm, "end": v(37.02, 13.3) * mm});
            skLineSegment(sketch, "E528", {"start": v(37.02, 13.3) * mm, "end": v(36.85, 12.4) * mm});
            skLineSegment(sketch, "E529", {"start": v(36.85, 12.4) * mm, "end": v(36.56, 11.77) * mm});
            skLineSegment(sketch, "E530", {"start": v(36.56, 11.77) * mm, "end": v(36.25, 11.12) * mm});
            skLineSegment(sketch, "E531", {"start": v(36.25, 11.12) * mm, "end": v(35.76, 10.05) * mm});
            skLineSegment(sketch, "E532", {"start": v(35.76, 10.05) * mm, "end": v(35.35, 9.22) * mm});
            skLineSegment(sketch, "E533", {"start": v(35.35, 9.22) * mm, "end": v(35.14, 8.56) * mm});
            skLineSegment(sketch, "E534", {"start": v(35.14, 8.56) * mm, "end": v(34.96, 8.03) * mm});
            skLineSegment(sketch, "E535", {"start": v(34.96, 8.03) * mm, "end": v(34.89, 7.62) * mm});
            skLineSegment(sketch, "E536", {"start": v(34.89, 7.62) * mm, "end": v(34.94, 7.24) * mm});
            skLineSegment(sketch, "E537", {"start": v(34.94, 7.24) * mm, "end": v(35.01, 6.75) * mm});
            skLineSegment(sketch, "E538", {"start": v(35.01, 6.75) * mm, "end": v(35.05, 6.23) * mm});
            skLineSegment(sketch, "E539", {"start": v(35.05, 6.23) * mm, "end": v(35.1, 5.78) * mm});
            skLineSegment(sketch, "E540", {"start": v(35.1, 5.78) * mm, "end": v(34.65, 4.92) * mm});
            skLineSegment(sketch, "E541", {"start": v(34.65, 4.92) * mm, "end": v(34.23, 4.46) * mm});
            skLineSegment(sketch, "E542", {"start": v(34.23, 4.46) * mm, "end": v(33.6, 4.13) * mm});
            skLineSegment(sketch, "E543", {"start": v(33.6, 4.13) * mm, "end": v(33.24, 3.9) * mm});
            skLineSegment(sketch, "E544", {"start": v(33.24, 3.9) * mm, "end": v(32.81, 3.73) * mm});
            skArc(sketch, "E545", {"start": v(19.92, 12.94) * mm, "mid": v(17.44, 10.98) * mm, "end": v(16.03, 8.16) * mm});
            skLineSegment(sketch, "E546", {"start": v(16.03, 8.89) * mm, "end": v(16.03, 8.16) * mm});
            skArc(sketch, "E547.trimOffspring", {"start": v(19.69, 13.83) * mm, "mid": v(17.13, 11.9) * mm, "end": v(16.03, 8.89) * mm});
            skArc(sketch, "E548", {"start": v(25.02, 15.93) * mm, "mid": v(21.75, 16.4) * mm, "end": v(19.69, 13.83) * mm});
            skArc(sketch, "E549", {"start": v(31.15, 13.46) * mm, "mid": v(28.34, 15.34) * mm, "end": v(25.02, 15.93) * mm});
            skArc(sketch, "E550", {"start": v(31.15, 13.46) * mm, "mid": v(28.35, 14.59) * mm, "end": v(25.38, 15.12) * mm});
            skArc(sketch, "E551", {"start": v(25.1, 13.22) * mm, "mid": v(25.44, 14.14) * mm, "end": v(25.38, 15.12) * mm});
            skArc(sketch, "E552", {"start": v(19.92, 12.94) * mm, "mid": v(20.45, 12.35) * mm, "end": v(21.21, 12.16) * mm});
            skLineSegment(sketch, "E553", {"start": v(21.21, 12.16) * mm, "end": v(21.43, 12.28) * mm});
            skLineSegment(sketch, "E554", {"start": v(21.43, 12.28) * mm, "end": v(21.58, 12.48) * mm});
            skLineSegment(sketch, "E555", {"start": v(21.58, 12.48) * mm, "end": v(21.58, 12.76) * mm});
            skLineSegment(sketch, "E556", {"start": v(21.58, 12.76) * mm, "end": v(21.4, 12.95) * mm});
            skLineSegment(sketch, "E557", {"start": v(21.4, 12.95) * mm, "end": v(21.14, 13.14) * mm});
            skLineSegment(sketch, "E558", {"start": v(21.14, 13.14) * mm, "end": v(20.96, 13.35) * mm});
            skLineSegment(sketch, "E559", {"start": v(20.96, 13.35) * mm, "end": v(20.87, 13.6) * mm});
            skLineSegment(sketch, "E560", {"start": v(20.87, 13.6) * mm, "end": v(20.93, 13.85) * mm});
            skLineSegment(sketch, "E561", {"start": v(20.93, 13.85) * mm, "end": v(21.15, 14) * mm});
            skLineSegment(sketch, "E562", {"start": v(21.15, 14) * mm, "end": v(21.46, 13.97) * mm});
            skLineSegment(sketch, "E563", {"start": v(21.46, 13.97) * mm, "end": v(21.77, 13.8) * mm});
            skLineSegment(sketch, "E564", {"start": v(21.77, 13.8) * mm, "end": v(22.02, 13.53) * mm});
            skLineSegment(sketch, "E565", {"start": v(22.02, 13.53) * mm, "end": v(22.16, 12.88) * mm});
            skLineSegment(sketch, "E566", {"start": v(22.16, 12.88) * mm, "end": v(22.16, 12.55) * mm});
            skLineSegment(sketch, "E567", {"start": v(22.16, 12.55) * mm, "end": v(22.15, 12.16) * mm});
            skLineSegment(sketch, "E568", {"start": v(22.15, 12.16) * mm, "end": v(22.28, 11.91) * mm});
            skLineSegment(sketch, "E569", {"start": v(22.28, 11.91) * mm, "end": v(22.45, 11.7) * mm});
            skLineSegment(sketch, "E570", {"start": v(22.45, 11.7) * mm, "end": v(22.73, 11.57) * mm});
            skLineSegment(sketch, "E571", {"start": v(22.73, 11.57) * mm, "end": v(22.98, 11.51) * mm});
            skLineSegment(sketch, "E572", {"start": v(22.98, 11.51) * mm, "end": v(23.23, 11.48) * mm});
            skLineSegment(sketch, "E573", {"start": v(23.23, 11.48) * mm, "end": v(23.38, 11.72) * mm});
            skLineSegment(sketch, "E574", {"start": v(23.38, 11.72) * mm, "end": v(22.97, 13.32) * mm});
            skLineSegment(sketch, "E575", {"start": v(22.97, 13.32) * mm, "end": v(23.88, 11.84) * mm});
            skLineSegment(sketch, "E576", {"start": v(23.88, 11.84) * mm, "end": v(24.1, 11.83) * mm});
            skLineSegment(sketch, "E577", {"start": v(24.1, 11.83) * mm, "end": v(24.3, 12) * mm});
            skLineSegment(sketch, "E578", {"start": v(24.3, 12) * mm, "end": v(24.47, 12.23) * mm});
            skLineSegment(sketch, "E579", {"start": v(24.47, 12.23) * mm, "end": v(24.62, 12.52) * mm});
            skLineSegment(sketch, "E580", {"start": v(24.62, 12.52) * mm, "end": v(24.64, 12.66) * mm});
            skLineSegment(sketch, "E581", {"start": v(24.64, 12.66) * mm, "end": v(24.52, 12.81) * mm});
            skLineSegment(sketch, "E582", {"start": v(24.52, 12.81) * mm, "end": v(24.33, 13.02) * mm});
            skLineSegment(sketch, "E583", {"start": v(24.33, 13.02) * mm, "end": v(23.98, 13.57) * mm});
            skLineSegment(sketch, "E584", {"start": v(23.98, 13.57) * mm, "end": v(23.82, 14.06) * mm});
            skLineSegment(sketch, "E585", {"start": v(23.82, 14.06) * mm, "end": v(23.82, 14.48) * mm});
            skLineSegment(sketch, "E586", {"start": v(23.82, 14.48) * mm, "end": v(23.99, 14.75) * mm});
            skLineSegment(sketch, "E587", {"start": v(23.99, 14.75) * mm, "end": v(24.26, 14.82) * mm});
            skLineSegment(sketch, "E588", {"start": v(24.26, 14.82) * mm, "end": v(24.53, 14.75) * mm});
            skLineSegment(sketch, "E589", {"start": v(24.53, 14.75) * mm, "end": v(24.6, 14.16) * mm});
            skLineSegment(sketch, "E590", {"start": v(24.6, 14.16) * mm, "end": v(24.6, 13.79) * mm});
            skLineSegment(sketch, "E591", {"start": v(24.6, 13.79) * mm, "end": v(24.6, 13.56) * mm});
            skLineSegment(sketch, "E592", {"start": v(24.6, 13.56) * mm, "end": v(24.67, 13.32) * mm});
            skLineSegment(sketch, "E593", {"start": v(24.67, 13.32) * mm, "end": v(24.87, 13.21) * mm});
            skLineSegment(sketch, "E594", {"start": v(24.87, 13.21) * mm, "end": v(25.1, 13.22) * mm});
            skPoint(sketch, "E595.10.internal.snap0", {"position": v(22.63, 5.72) * mm});
            skFitSpline(sketch, "E595", {"points": [v(21.65, 0.94) * mm, v(21.96, 1.99) * mm, v(22.43, 3.2) * mm, v(22.83, 4.2) * mm, v(23.47, 5.28) * mm, v(24.12, 5.97) * mm, v(24.92, 6.47) * mm, v(25.56, 6.67) * mm, v(26.7, 6.67) * mm, v(27.91, 6.23) * mm, v(28.81, 5.72) * mm, v(29.61, 5.08) * mm, v(30.22, 4.5) * mm, v(30.7, 3.82) * mm, v(30.87, 3.14) * mm, v(30.53, 2.5) * mm, v(29.74, 2.19) * mm, v(28.62, 1.94) * mm, v(27.36, 1.85) * mm, v(26.25, 1.77) * mm, v(25.11, 1.5) * mm, v(24.23, 1.22) * mm, v(23.16, 0.9) * mm, v(22.27, 0.8) * mm, v(21.65, 0.94) * mm]});
            skFitSpline(sketch, "E596", {"points": [v(12.96, 27.65) * mm, v(13.38, 28.26) * mm, v(14.15, 28.73) * mm, v(15.19, 28.89) * mm, v(16.62, 28.74) * mm, v(17.2, 28.11) * mm, v(17.45, 27.24) * mm, v(17.31, 25.88) * mm, v(17.34, 24.72) * mm, v(17.7, 23.71) * mm, v(18.1, 23.2) * mm, v(18.51, 22.73) * mm, v(17.95, 22.84) * mm, v(17.26, 23.44) * mm, v(16.83, 24.23) * mm, v(16.62, 25.19) * mm, v(16.5, 26.32) * mm, v(16.36, 27.2) * mm, v(15.94, 27.82) * mm, v(15.16, 28.15) * mm, v(14.24, 28.17) * mm, v(13.46, 27.97) * mm, v(12.96, 27.65) * mm]});
            skFitSpline(sketch, "E597", {"points": [v(19.2, 30.28) * mm, v(19.9, 30.3) * mm, v(20.69, 30.13) * mm, v(21.16, 29.7) * mm, v(21.2, 28.95) * mm, v(21.06, 28.1) * mm, v(20.76, 27.26) * mm, v(20.58, 26.44) * mm, v(20.45, 25.76) * mm, v(20.6, 25.28) * mm, v(20.78, 24.68) * mm, v(20.32, 24.96) * mm, v(20.13, 25.8) * mm, v(20.07, 26.9) * mm, v(20.1, 27.82) * mm, v(19.98, 28.7) * mm, v(19.8, 29.39) * mm, v(19.51, 29.9) * mm, v(19.2, 30.28) * mm]});
            skFitSpline(sketch, "E598", {"points": [v(26.5, 31.82) * mm, v(25.94, 31.18) * mm, v(25.74, 30.58) * mm, v(25.87, 30.1) * mm, v(26.75, 29.92) * mm, v(27.85, 29.9) * mm, v(29.42, 29.64) * mm, v(30.68, 29.07) * mm, v(31.8, 28.26) * mm, v(32.77, 27.23) * mm, v(33.62, 26.12) * mm, v(34.28, 24.9) * mm, v(34.88, 23.68) * mm, v(35.74, 22.3) * mm, v(36.7, 21.12) * mm, v(37.65, 20.72) * mm, v(38.49, 21.05) * mm, v(38.9, 21.83) * mm, v(38.93, 22.77) * mm, v(38.75, 23.9) * mm, v(39.06, 25.17) * mm, v(39.46, 26.27) * mm, v(39.78, 27.28) * mm, v(39.37, 28.58) * mm, v(38.59, 29.35) * mm, v(37.23, 30.08) * mm, v(35.77, 30.67) * mm, v(34.44, 31.1) * mm, v(32.82, 31.59) * mm, v(31.49, 31.88) * mm, v(30.2, 32.1) * mm, v(28.67, 32.18) * mm, v(27.4, 32.09) * mm, v(26.5, 31.82) * mm]});
            skSolve(sketch);
        }
        {
            var Q0;
            Q0=makeQuery(id+"F0.imprint","IMPRINT",FACE,{"disambiguationData":[TD([[makeQuery(id+"F0.imprint","IMPRINT",EDGE,{"derivedFrom":sQuery(id+"F0.wireOp",EDGE,"E53")}),1.0]])]});
            var Q1;
            Q1=makeQuery(id+"F0.imprint","IMPRINT",FACE,{"disambiguationData":[TD([[makeQuery(id+"F0.imprint","IMPRINT",EDGE,{"derivedFrom":sQuery(id+"F0.wireOp",EDGE,"E595")}),-1.0]])]});
            var Q2;
            Q2=makeQuery(id+"F0.imprint","IMPRINT",FACE,{"disambiguationData":[TD([[makeQuery(id+"F0.imprint","IMPRINT",EDGE,{"derivedFrom":sQuery(id+"F0.wireOp",EDGE,"E0")}),-1.0]])]});
            var Q3;
            Q3=makeQuery(id+"F0.imprint","IMPRINT",FACE,{"disambiguationData":[TD([[makeQuery(id+"F0.imprint","IMPRINT",EDGE,{"derivedFrom":sQuery(id+"F0.wireOp",EDGE,"E596")}),-1.0]])]});
            var Q4;
            Q4=makeQuery(id+"F0.imprint","IMPRINT",FACE,{"disambiguationData":[TD([[makeQuery(id+"F0.imprint","IMPRINT",EDGE,{"derivedFrom":sQuery(id+"F0.wireOp",EDGE,"E597")}),-1.0]])]});
            var Q5;
            Q5=makeQuery(id+"F0.imprint","IMPRINT",FACE,{"disambiguationData":[TD([[makeQuery(id+"F0.imprint","IMPRINT",EDGE,{"derivedFrom":sQuery(id+"F0.wireOp",EDGE,"E598")}),1.0]])]});
            extrude(context, id + "F1", {"entities" : qUnion([Q0, Q1, Q2, Q3, Q4, Q5]), "depth" : 2 * mm, "offsetDistance" : 25 * mm});
        }
        {
            var Q0;
            Q0=qCreatedBy(makeId("Top.planeOp"),FACE);
            var sketch = newSketch(context, id + "F2", { "sketchPlane" : qUnion([Q0])});
            skText(sketch, "E599", { "text": "STEFF", "fontName": "OpenSans-Bold.ttf"});
            const initialGuessF2  = {"E599": [0.00485, -0.01072, 1, 0, 0.00923]};
            skSetInitialGuess(sketch, initialGuessF2);
            skSolve(sketch);
        }
        {
            var Q0;
            Q0 = qSketchRegion(id + "F2", true);
            extrude(context, id + "F3", {"entities" : qUnion([Q0]), "depth" : 2 * mm, "offsetDistance" : 25 * mm});
        }
    });
